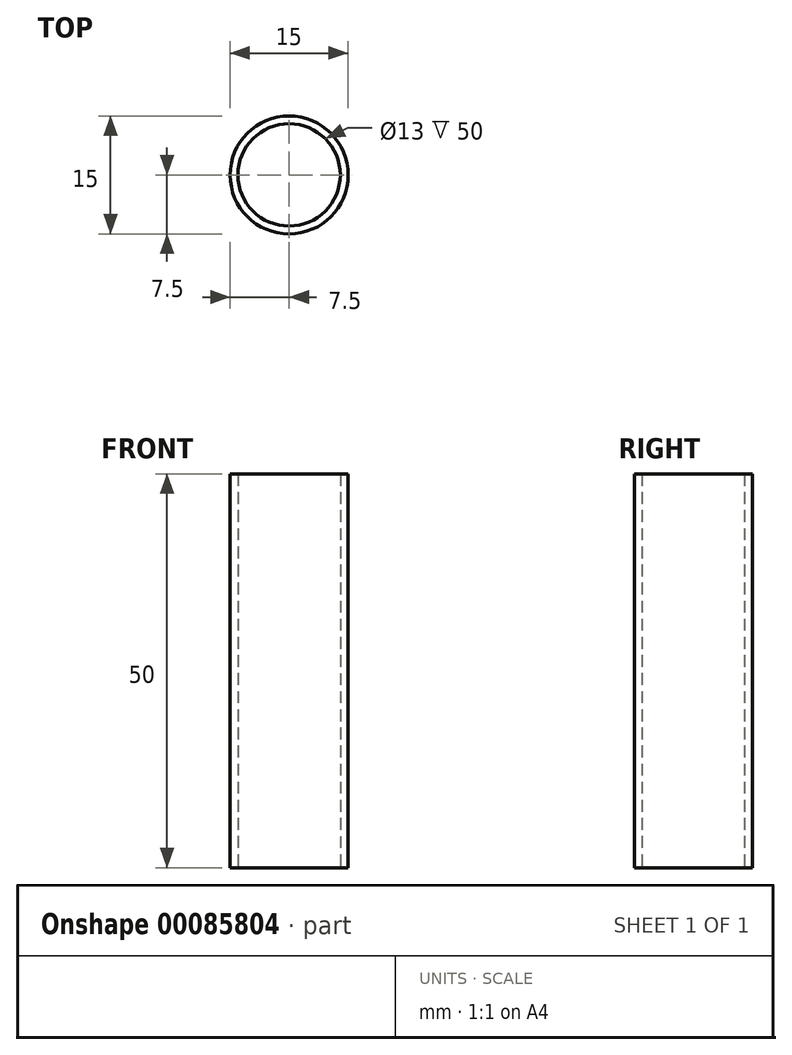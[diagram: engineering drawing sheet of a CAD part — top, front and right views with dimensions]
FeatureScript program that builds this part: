
annotation { "Feature Type Name" : "Feature", "Feature Type Description" : "" }
export const myFeature = defineFeature(function(context is Context, id is Id, definition is map)
    precondition{}
    {
        {
            var Q0;
            Q0=qCreatedBy(makeId("Top.planeOp"),FACE);
            var sketch = newSketch(context, id + "F0", { "sketchPlane" : qUnion([Q0])});
            skCircle(sketch, "E0", {"center": v(0, 0) * mm, "radius": 6.5 * mm});
            skCircle(sketch, "E1.0", {"center": v(0, 0) * mm, "radius": 7.5 * mm});
            skSolve(sketch);
        }
        {
            var Q0;
            Q0=makeQuery(id+"F0.imprint","IMPRINT",FACE,{"disambiguationData":[TD([[makeQuery(id+"F0.imprint","IMPRINT",EDGE,{"derivedFrom":sQuery(id+"F0.wireOp",EDGE,"E0")}),-1.0]])]});
            extrude(context, id + "F1", {"entities" : qUnion([Q0]), "depth" : 50 * mm});
        }
    });
